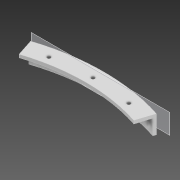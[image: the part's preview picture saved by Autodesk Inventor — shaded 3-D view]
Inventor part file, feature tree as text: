
AUTODESK INVENTOR PART (.ipt)
format: ipt  version: 2020 (Build 240168000, 168)  size: 157,696 bytes
history: native  units: in
note: dims shown in document units (in); Inventor stores cm internally (conversion verified against a paired STEP export)
features: extrude x4, sketch x4, plane x1
ambient origin geometry x8: Origin, YZ Plane, XZ Plane, XY Plane, X Axis, Y Axis, Z Axis, Center Point
bodies: Solid1 (feature_tree)
feature tree (9):
  extrude  "Extrusion1"  Depth=0.7421in
  extrude  "Extrusion2"  Depth=0.1181in
  extrude  "Extrusion3"  Depth=0.1181in
  plane  "Work Plane1"
  extrude  "Extrusion4"  Depth=0.3937in
  sketch  "Sketch1"  dims[d0=15.748in d1=0.7421in]
  sketch  "Sketch3"  dims[d2=0.4947in d4=0.1181in]
  sketch  "Sketch4"  dims[d5=0.1181in d6=0.1181in]
  sketch  "Sketch6"  dims[d7=0.1181in d8=0.5906in d9=0.0in d10=0.0in d12=0.7087in d13=0.7087in d14=0.7087in d15=0.1181in d16=0.0in d17=0.1181in d18=0.2953in d19=0.1378in d20=0.1181in d21=0.0in d22=-7.874in d23=0.1181in d24=0.2953in d25=0.1378in d26=0.3937in d27=0.0in d28=0.1181in d29=0.2953in d30=0.1181in d31=0.2953in d32=1.5748in d33=1.5748in d34=0.1378in d35=0.1378in d36=1.5748in d37=3.1496in d38=0.1378in d39=0.1378in]
